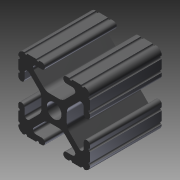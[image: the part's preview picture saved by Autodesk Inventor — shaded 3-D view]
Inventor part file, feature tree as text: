
AUTODESK INVENTOR PART (.ipt)
format: ipt  version: 2011 SP1 (Build 150282100, 282)  size: 195,072 bytes
history: native  units: in
note: dims shown in document units (in); Inventor stores cm internally (conversion verified against a paired STEP export)
features: other x21, extrude x1, sketch x1
ambient origin geometry x8: Origin, YZ Plane, XZ Plane, XY Plane, X Axis, Y Axis, Z Axis, Center Point
bodies: Solid1 (feature_tree)
feature tree (23):
  extrude  "Extrusion1"  [1 undecoded]
  other  "b1_XY"
  other  "b1_YZ"
  other  "b1_ZX"
  other  "b1_X"
  other  "b1_Y"
  other  "b1_Z"
  other  "b1_Center"
  other  "b2_XY"
  other  "b2_YZ"
  other  "b2_ZX"
  other  "b2_X"
  other  "b2_Y"
  other  "b2_Z"
  other  "b2_Center"
  other  "profile1010_XY"
  other  "profile1010_YZ"
  other  "profile1010_ZX"
  other  "profile1010_X"
  other  "profile1010_Y"
  other  "profile1010_Z"
  other  "profile1010_Center"
  sketch  "Sketch_1"  dims[d0=1.0in d1=0.0in]
note: 1 required parameter value undecoded (feature->parameter linkage not recoverable at this tier; creation-order binding heuristic only, values carry confidence <= 0.55)
